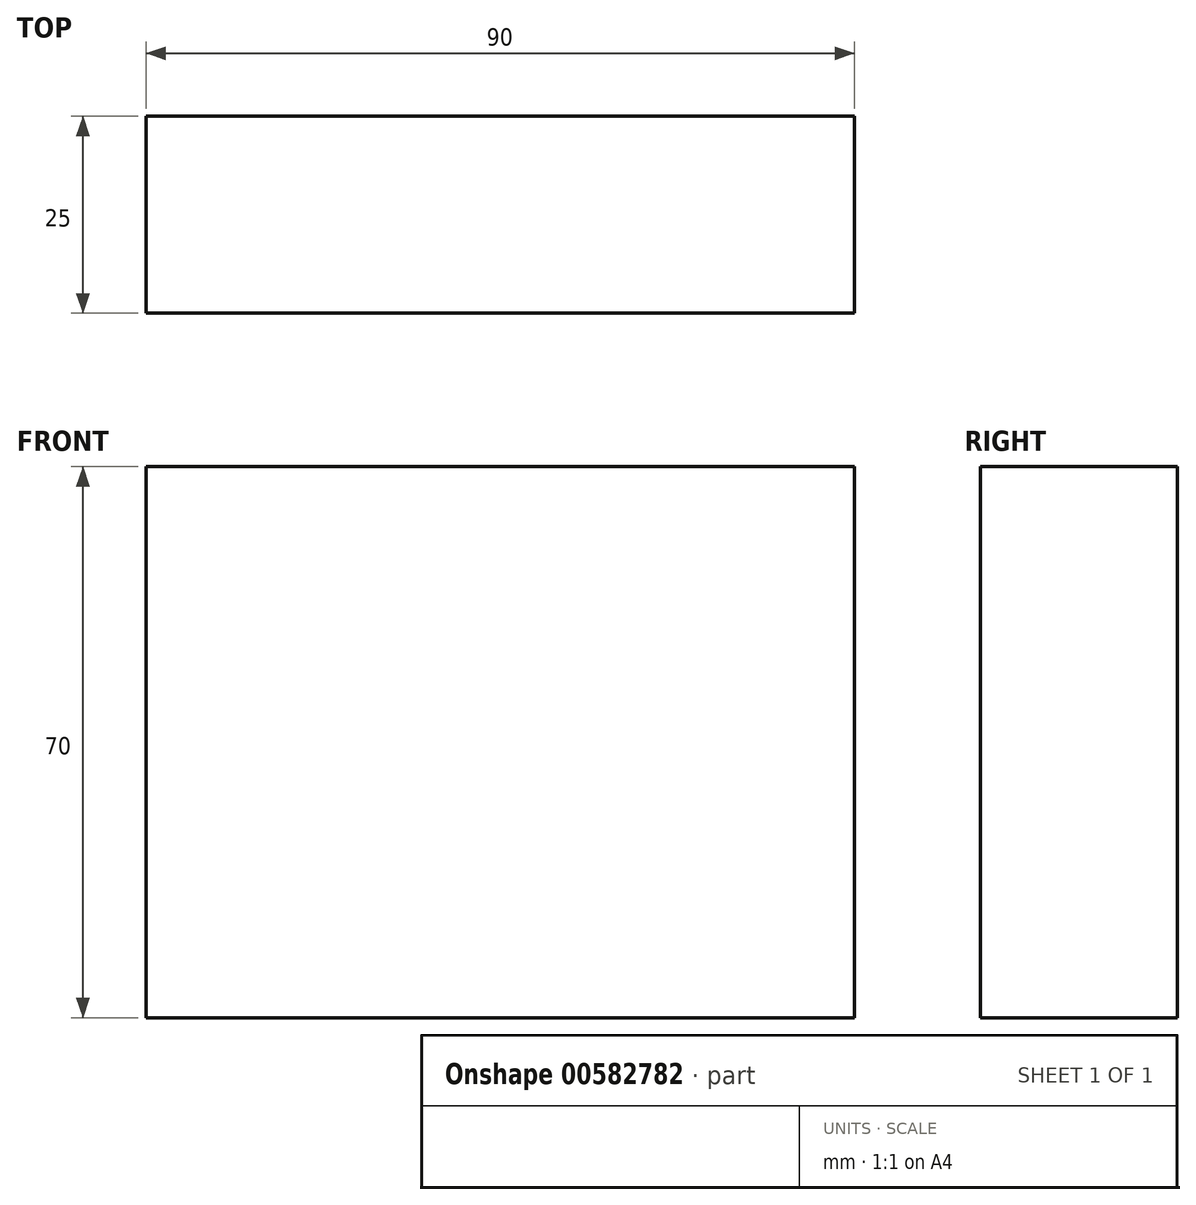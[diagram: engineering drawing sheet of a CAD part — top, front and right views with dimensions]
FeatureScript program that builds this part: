
annotation { "Feature Type Name" : "Feature", "Feature Type Description" : "" }
export const myFeature = defineFeature(function(context is Context, id is Id, definition is map)
    precondition{}
    {
        {
            var Q0;
            Q0=qCreatedBy(makeId("Front.planeOp"),FACE);
            var sketch = newSketch(context, id + "F0", { "sketchPlane" : qUnion([Q0])});
            skLineSegment(sketch, "E0.bottom", {"start": v(45, 35) * mm, "end": v(-45, 35) * mm});
            skLineSegment(sketch, "E0.top", {"start": v(45, -35) * mm, "end": v(-45, -35) * mm});
            skLineSegment(sketch, "E0.left", {"start": v(45, 35) * mm, "end": v(45, -35) * mm});
            skLineSegment(sketch, "E0.right", {"start": v(-45, 35) * mm, "end": v(-45, -35) * mm});
            skPoint(sketch, "E0.middle", {"position": v(0, 0) * mm});
            skSolve(sketch);
        }
        {
            var Q0;
            Q0=makeQuery(id+"F0.imprint","IMPRINT",FACE,{"disambiguationData":[TD([[makeQuery(id+"F0.imprint","IMPRINT",EDGE,{"derivedFrom":sQuery(id+"F0.wireOp",EDGE,"E0.bottom")}),1.0]])]});
            extrude(context, id + "F1", {"entities" : qUnion([Q0]), "endBound" : BoundingType.SYMMETRIC, "oppositeDirection" : true, "depth" : 25 * mm, "offsetDistance" : 25 * mm});
        }
    });
